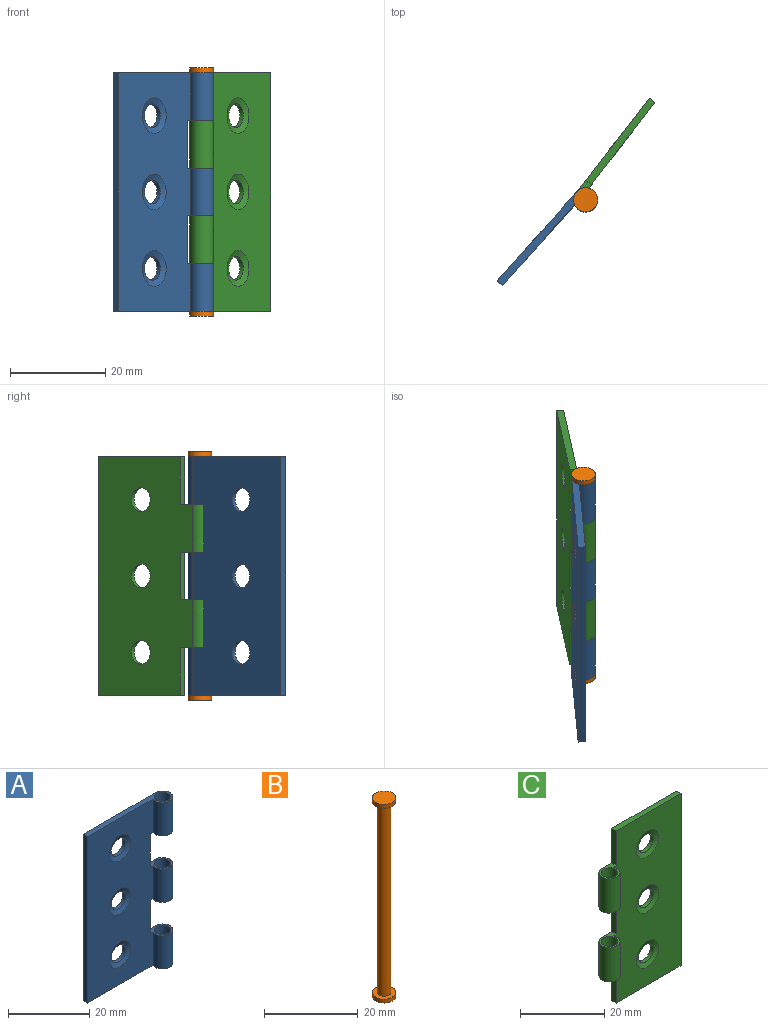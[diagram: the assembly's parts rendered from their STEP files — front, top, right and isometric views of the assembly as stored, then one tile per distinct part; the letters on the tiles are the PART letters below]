
ASSEMBLY  parts=3 mates=2
PART A: 23 faces, bbox 27.5x5x50 mm
  f0: plane 50x22.71mm, normal (0,-1,0), area 983.7mm2, adj f2,f3,f4,f6,f8,f10,f11,f12
  f1: plane 50x25mm, normal (0,1,0), area 1126.1mm2, adj f2,f3,f4,f5,f7,f9,f11,f12
  f2: plane 50x1.5mm, normal (-1,0,0), area 75mm2, adj f0,f1,f3,f4
  f3: plane 27.5x5mm, normal (0,0,1), area 42.1mm2, adj f0,f1,f2,f19,f21
  f4: plane 27.5x5mm, normal (0,0,-1), area 42.1mm2, adj f0,f1,f2,f17,f22
  f5: cylinder r=2.5mm len=5mm, axis (0,-1,0), area 15.4mm2, adj f1,f6
  f6: cone r=2.5mm half-angle=67.5deg, axis (0,-1,0), area 26.6mm2, adj f0,f5
  f7: cylinder r=2.5mm len=5mm, axis (0,-1,0), area 15.4mm2, adj f1,f8
  f8: cone r=2.5mm half-angle=67.5deg, axis (0,-1,0), area 26.6mm2, adj f0,f7
  f9: cylinder r=2.5mm len=5mm, axis (0,-1,0), area 15.4mm2, adj f1,f10
  f10: cone r=2.5mm half-angle=67.5deg, axis (0,-1,0), area 26.6mm2, adj f0,f9
  f11: plane 5.75x5mm, normal (0,0,-1), area 9.5mm2, adj f0,f1,f13,f18,f20
  f12: plane 5.75x5mm, normal (0,0,1), area 9.5mm2, adj f0,f1,f13,f17,f22
  f13: plane 10x1.5mm, normal (1,0,0), area 15mm2, adj f0,f1,f11,f12
  f14: plane 5.75x5mm, normal (0,0,-1), area 9.5mm2, adj f0,f1,f16,f19,f21
  f15: plane 5.75x5mm, normal (0,0,1), area 9.5mm2, adj f0,f1,f16,f18,f20
  f16: plane 10x1.5mm, normal (1,0,0), area 15mm2, adj f0,f1,f14,f15
  f17: cylinder r=2.5mm len=10mm, axis (0,0,-1), area 128.1mm2, adj f0,f1,f4,f12
  f18: cylinder r=2.5mm len=10mm, axis (0,0,-1), area 128.1mm2, adj f0,f1,f11,f15
  f19: cylinder r=2.5mm len=10mm, axis (0,0,-1), area 128.1mm2, adj f0,f1,f3,f14
  f20: cylinder r=2mm len=10mm, axis (0,0,-1), area 125.7mm2, adj f11,f15
  f21: cylinder r=2mm len=10mm, axis (0,0,-1), area 125.7mm2, adj f3,f14
  f22: cylinder r=2mm len=10mm, axis (0,0,-1), area 125.7mm2, adj f4,f12
PART B: 7 faces, bbox 5x5x52 mm
  f0: cylinder r=1.43mm len=50mm, axis (0,0,-1), area 447.7mm2, adj f3,f5
  f1: cylinder r=2.5mm len=5mm, axis (0,0,1), area 15.7mm2, adj f2,f3
  f2: plane 5x5mm, normal (0,0,-1), area 19.6mm2, adj f1
  f3: plane 5x5mm, normal (0,0,1), area 13.3mm2, adj f0,f1
  f4: cylinder r=2.5mm len=5mm, axis (0,0,1), area 15.7mm2, adj f5,f6
  f5: plane 5x5mm, normal (0,0,-1), area 13.3mm2, adj f0,f4
  f6: plane 5x5mm, normal (0,0,1), area 19.6mm2, adj f4
PART C: 22 faces, bbox 27.5x5x50 mm
  f0: plane 50x22.71mm, normal (0,-1,0), area 974.1mm2, adj f2,f3,f4,f6,f8,f10,f11,f12
  f1: plane 50x25mm, normal (0,1,0), area 1093.6mm2, adj f2,f3,f4,f5,f7,f9,f11,f12
  f2: plane 50x1.5mm, normal (1,0,0), area 75mm2, adj f0,f1,f3,f4
  f3: plane 21.75x1.5mm, normal (0,0,1), area 32.6mm2, adj f0,f1,f2,f16
  f4: plane 21.75x1.5mm, normal (0,0,-1), area 32.6mm2, adj f0,f1,f2,f12
  f5: cylinder r=2.5mm len=5mm, axis (0,-1,0), area 15.4mm2, adj f1,f6
  f6: cone r=2.5mm half-angle=67.5deg, axis (0,-1,0), area 26.6mm2, adj f0,f5
  f7: cylinder r=2.5mm len=5mm, axis (0,-1,0), area 15.4mm2, adj f1,f8
  f8: cone r=2.5mm half-angle=67.5deg, axis (0,-1,0), area 26.6mm2, adj f0,f7
  f9: cylinder r=2.5mm len=5mm, axis (0,-1,0), area 15.4mm2, adj f1,f10
  f10: cone r=2.5mm half-angle=67.5deg, axis (0,-1,0), area 26.6mm2, adj f0,f9
  f11: plane 5.75x5mm, normal (0,0,-1), area 9.5mm2, adj f0,f1,f12,f19,f21
  f12: plane 10x1.5mm, normal (-1,0,0), area 15mm2, adj f0,f1,f4,f11
  f13: plane 5.75x5mm, normal (0,0,-1), area 9.5mm2, adj f0,f1,f14,f18,f20
  f14: plane 10x1.5mm, normal (-1,0,0), area 15mm2, adj f0,f1,f13,f15
  f15: plane 5.75x5mm, normal (0,0,1), area 9.5mm2, adj f0,f1,f14,f19,f21
  f16: plane 10x1.5mm, normal (-1,0,0), area 15mm2, adj f0,f1,f3,f17
  f17: plane 5.75x5mm, normal (0,0,1), area 9.5mm2, adj f0,f1,f16,f18,f20
  f18: cylinder r=2.5mm len=10mm, axis (0,0,-1), area 128.1mm2, adj f0,f1,f13,f17
  f19: cylinder r=2.5mm len=10mm, axis (0,0,-1), area 128.1mm2, adj f0,f1,f11,f15
  f20: cylinder r=2mm len=10mm, axis (0,0,-1), area 125.7mm2, adj f13,f17
  f21: cylinder r=2mm len=10mm, axis (0,0,-1), area 125.7mm2, adj f11,f15
PLACE A rot(axis=(0,0,1),48.2deg) t=(-11.28,3.9,-5.24)mm fixed
PLACE B t=(-11.28,3.9,-5.24)mm
PLACE C rot(axis=(0,0,1),52.3deg) t=(-11.28,3.9,-5.24)mm
MATE revolute C.f18 <-> B.f0  axis (0,0,-1) through (-11.28,3.9,9.76)mm
MATE revolute B.f0 <-> A.f17  axis (0,0,-1) through (-11.28,3.9,19.76)mm
